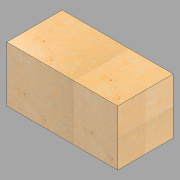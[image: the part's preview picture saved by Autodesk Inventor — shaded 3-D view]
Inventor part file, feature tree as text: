
AUTODESK INVENTOR PART (.ipt)
format: ipt  version: 2022.1 (Build 261234020, 234B)  size: 125,952 bytes
history: native  units: in
note: dims shown in document units (in); Inventor stores cm internally (conversion verified against a paired STEP export)
features: extrude x1, sketch x1
ambient origin geometry x8: Origin, YZ Plane, XZ Plane, XY Plane, X Axis, Y Axis, Z Axis, Center Point
bodies: Solid1 (feature_tree)
feature tree (2):
  extrude  "Extrusion1"  Depth=24.0in
  sketch  "Sketch1"  dims[d0=24.0in d1=24.0in d2=48.0in d3=0.0in]
